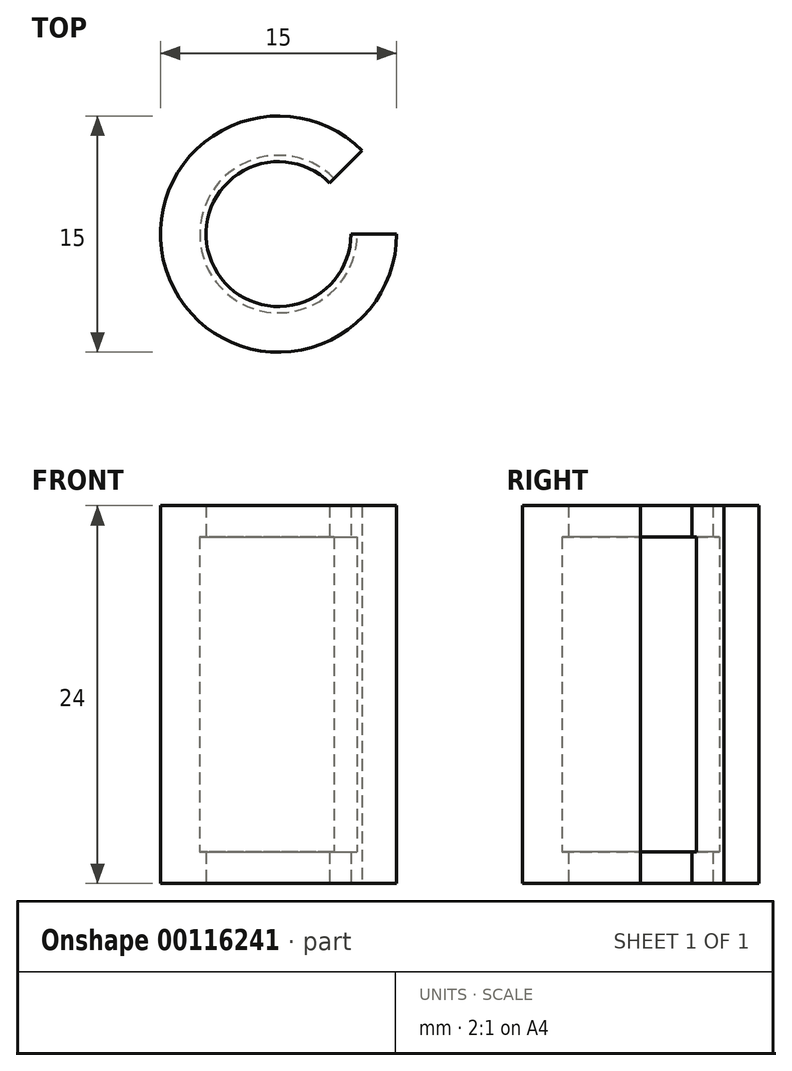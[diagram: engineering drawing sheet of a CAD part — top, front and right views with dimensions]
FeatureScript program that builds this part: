
annotation { "Feature Type Name" : "Feature", "Feature Type Description" : "" }
export const myFeature = defineFeature(function(context is Context, id is Id, definition is map)
    precondition{}
    {
        {
            var Q0;
            Q0=qCreatedBy(makeId("Top.planeOp"),FACE);
            var sketch = newSketch(context, id + "F0", { "sketchPlane" : qUnion([Q0])});
            skCircle(sketch, "E0", {"center": v(0, 0) * mm, "radius": 7.5 * mm});
            skCircle(sketch, "E1", {"center": v(0, 0) * mm, "radius": 5 * mm});
            skLineSegment(sketch, "E2", {"start": v(0, 0) * mm, "end": v(0, 14.87) * mm, "construction": true});
            skLineSegment(sketch, "E3", {"start": v(0, 0) * mm, "end": v(14.04, 0) * mm, "construction": true});
            skLineSegment(sketch, "E4", {"start": v(0, 0) * mm, "end": v(9.73, 9.73) * mm, "construction": true});
            skLineSegment(sketch, "E5", {"start": v(5.3, 5.3) * mm, "end": v(3.54, 3.54) * mm});
            skLineSegment(sketch, "E6", {"start": v(5, 0) * mm, "end": v(7.5, 0) * mm});
            skLineSegment(sketch, "E7", {"start": v(7.5, 0) * mm, "end": v(10.35, 1.75) * mm});
            skLineSegment(sketch, "E8", {"start": v(10.35, 1.75) * mm, "end": v(7.33, 5.52) * mm});
            skLineSegment(sketch, "E9", {"start": v(7.33, 5.52) * mm, "end": v(5.3, 5.3) * mm});
            skCircle(sketch, "E10", {"center": v(0, 0) * mm, "radius": 4.6 * mm});
            skLineSegment(sketch, "E11", {"start": v(3.54, 3.54) * mm, "end": v(2.46, 2.46) * mm});
            skLineSegment(sketch, "E12", {"start": v(2.46, 2.46) * mm, "end": v(2.97, 0) * mm});
            skLineSegment(sketch, "E13", {"start": v(2.97, 0) * mm, "end": v(5, 0) * mm});
            skSolve(sketch);
        }
        {
            var Q0;
            {var subQ0=sQuery(id+"F0.wireOp",EDGE,"E5");Q0=makeQuery(id+"F0.imprint","IMPRINT",FACE,{"disambiguationData":[TD([[makeQuery(id+"F0.imprint","IMPRINT",EDGE,{"derivedFrom":subQ0}),-1.0]])]});}
            var Q1;
            {var subQ0=sQuery(id+"F0.wireOp",EDGE,"E11");var subQ5=sQuery(id+"F0.wireOp",EDGE,"E10");var subQ6=makeQuery(id+"F0.imprint","INTERSECT",VERTEX,{"derivedFrom":[subQ5,subQ0]});Q1=makeQuery(id+"F0.imprint","IMPRINT",FACE,{"disambiguationData":[TD([[makeQuery(id+"F0.imprint","IMPRINT",EDGE,{"disambiguationData":[TD([[subQ6,-1.0]])],"derivedFrom":subQ5}),-1.0]])]});}
            extrude(context, id + "F1", {"entities" : qUnion([Q0, Q1]), "depth" : 2 * mm});
        }
        {
            var Q0;
            Q0=makeQuery(id+"F1.opExtrude","CAP_FACE",FACE,{"disambiguationData":[OSD([sQuery(id+"F0.wireOp",EDGE,"E0"),sQuery(id+"F0.wireOp",EDGE,"E5"),sQuery(id+"F0.wireOp",EDGE,"E6"),sQuery(id+"F0.wireOp",EDGE,"E10"),sQuery(id+"F0.wireOp",EDGE,"E11"),sQuery(id+"F0.wireOp",EDGE,"E13")])],"isStart":false});
            var sketch = newSketch(context, id + "F2", { "sketchPlane" : qUnion([Q0])});
            skCircle(sketch, "E14", {"center": v(0, 0) * mm, "radius": 5 * mm});
            skCircle(sketch, "E15", {"center": v(0, 0) * mm, "radius": 7.5 * mm});
            skLineSegment(sketch, "E16", {"start": v(3.54, 3.54) * mm, "end": v(5.3, 5.3) * mm});
            skLineSegment(sketch, "E17", {"start": v(5, 0) * mm, "end": v(7.5, 0) * mm});
            skSolve(sketch);
        }
        {
            var Q0;
            {var subQ0=sQuery(id+"F2.wireOp",EDGE,"E16");Q0=makeQuery(id+"F2.imprint","IMPRINT",FACE,{"disambiguationData":[TD([[makeQuery(id+"F2.imprint","IMPRINT",EDGE,{"derivedFrom":subQ0}),-1.0]])]});}
            extrude(context, id + "F3", {"entities" : qUnion([Q0]), "operationType" : NewBodyOperationType.ADD, "depth" : 20 * mm});
        }
        {
            var Q0;
            Q0=makeQuery(id+"F3.opExtrude","CAP_FACE",FACE,{"disambiguationData":[OSD([sQuery(id+"F2.wireOp",EDGE,"E14"),sQuery(id+"F2.wireOp",EDGE,"E15"),sQuery(id+"F2.wireOp",EDGE,"E16"),sQuery(id+"F2.wireOp",EDGE,"E17")])],"isStart":false});
            var sketch = newSketch(context, id + "F4", { "sketchPlane" : qUnion([Q0])});
            skCircle(sketch, "E18", {"center": v(0, 0) * mm, "radius": 7.5 * mm});
            skCircle(sketch, "E19", {"center": v(0, 0) * mm, "radius": 4.6 * mm});
            skLineSegment(sketch, "E20", {"start": v(5.3, 5.3) * mm, "end": v(0, 0) * mm});
            skLineSegment(sketch, "E21", {"start": v(0, 0) * mm, "end": v(7.5, 0) * mm});
            skSolve(sketch);
        }
        {
            var Q0;
            {var subQ5=makeQuery(id+"F3.opExtrude","CAP_EDGE",EDGE,{"disambiguationData":[OSD([sQuery(id+"F2.wireOp",EDGE,"E14")])],"isStart":false});Q0=makeQuery(id+"F4.imprint","IMPRINT",FACE,{"disambiguationData":[TD([[makeQuery(id+"F4.imprint","IMPRINT",EDGE,{"derivedFrom":subQ5}),-1.0]])]});}
            var Q1;
            {var subQ5=makeQuery(id+"F3.opExtrude","CAP_EDGE",EDGE,{"disambiguationData":[OSD([sQuery(id+"F2.wireOp",EDGE,"E14")])],"isStart":false});Q1=makeQuery(id+"F4.imprint","IMPRINT",FACE,{"disambiguationData":[TD([[makeQuery(id+"F4.imprint","IMPRINT",EDGE,{"derivedFrom":subQ5}),1.0]])]});}
            extrude(context, id + "F5", {"entities" : qUnion([Q0, Q1]), "operationType" : NewBodyOperationType.ADD, "depth" : 2 * mm});
        }
    });
